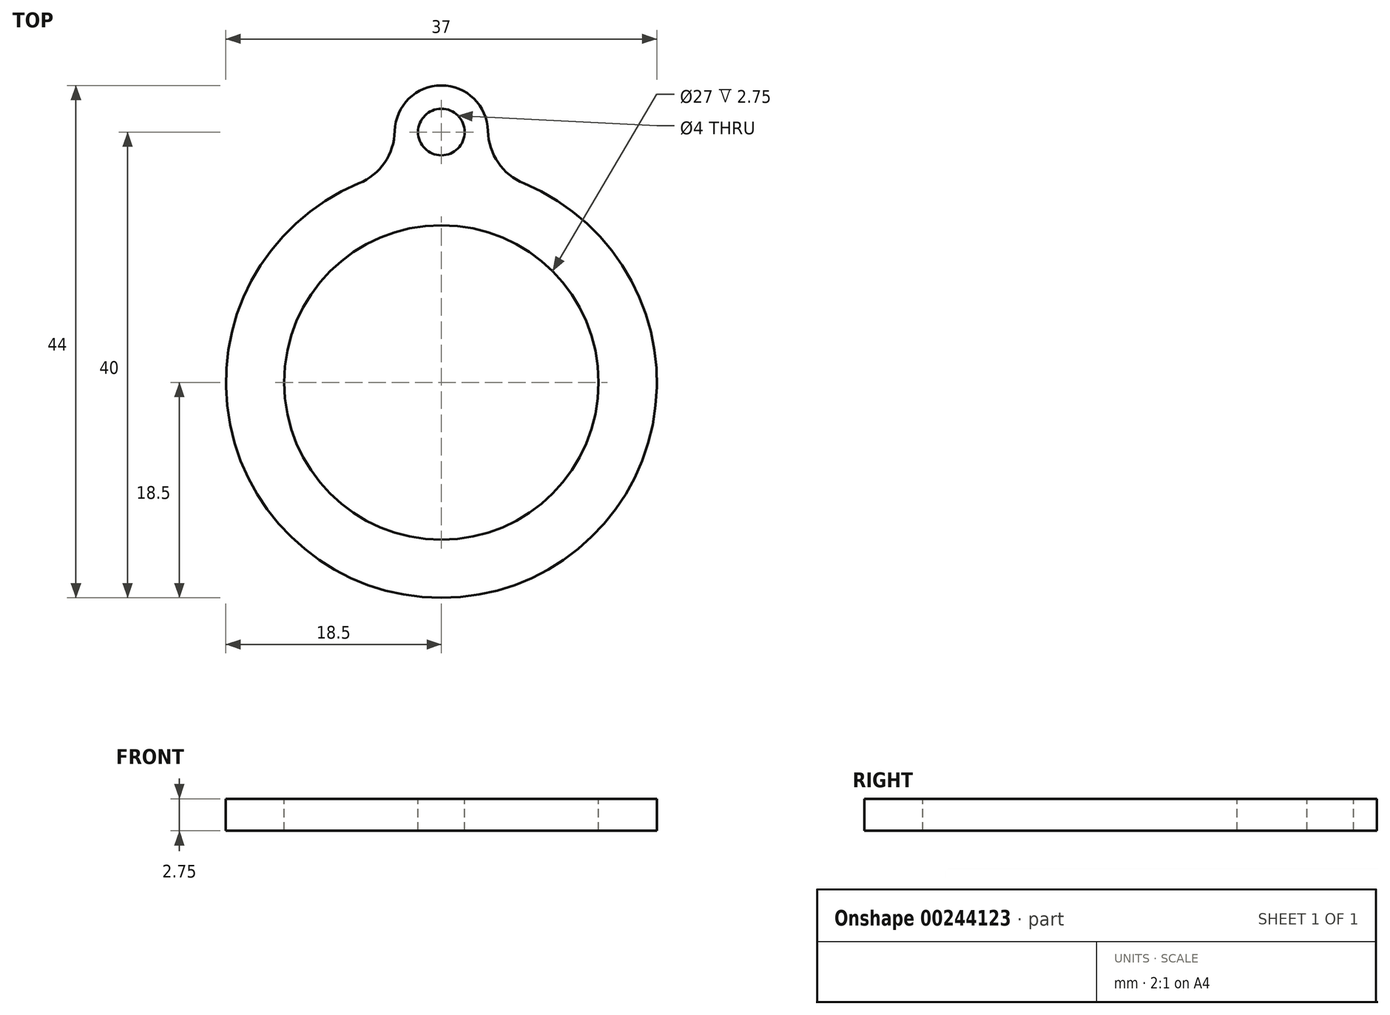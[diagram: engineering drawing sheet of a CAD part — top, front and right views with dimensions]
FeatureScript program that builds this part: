
annotation { "Feature Type Name" : "Feature", "Feature Type Description" : "" }
export const myFeature = defineFeature(function(context is Context, id is Id, definition is map)
    precondition{}
    {
        {
            var Q0;
            Q0=qCreatedBy(makeId("Top.planeOp"),FACE);
            var sketch = newSketch(context, id + "F0", { "sketchPlane" : qUnion([Q0])});
            skCircle(sketch, "E0", {"center": v(0, 0) * mm, "radius": 18.5 * mm});
            skCircle(sketch, "E1", {"center": v(0, 0) * mm, "radius": 13.5 * mm});
            skCircle(sketch, "E2", {"center": v(0, 21.5) * mm, "radius": 4 * mm});
            skLineSegment(sketch, "E3", {"start": v(4, 21.5) * mm, "end": v(4, 18.06) * mm});
            skLineSegment(sketch, "E4", {"start": v(-4, 21.5) * mm, "end": v(-4, 18.06) * mm});
            skCircle(sketch, "E5", {"center": v(0, 21.5) * mm, "radius": 2 * mm});
            skSolve(sketch);
        }
        {
            var Q0;
            Q0=makeQuery(id+"F0.imprint","IMPRINT",FACE,{"disambiguationData":[TD([[makeQuery(id+"F0.imprint","IMPRINT",EDGE,{"derivedFrom":sQuery(id+"F0.wireOp",EDGE,"E1")}),-1.0]])]});
            var Q1;
            {var subQ0=sQuery(id+"F0.wireOp",EDGE,"E2");var subQ1=sQuery(id+"F0.wireOp",EDGE,"E0");var subQ2=makeQuery(id+"F0.imprint","INTERSECT",VERTEX,{"disambiguationData":[OD(0.0)],"derivedFrom":[subQ1,subQ0]});Q1=makeQuery(id+"F0.imprint","IMPRINT",FACE,{"disambiguationData":[TD([[makeQuery(id+"F0.imprint","IMPRINT",EDGE,{"disambiguationData":[TD([[subQ2,-1.0]])],"derivedFrom":subQ1}),1.0]])]});}
            var Q2;
            Q2=makeQuery(id+"F0.imprint","IMPRINT",FACE,{"disambiguationData":[TD([[makeQuery(id+"F0.imprint","IMPRINT",EDGE,{"derivedFrom":sQuery(id+"F0.wireOp",EDGE,"E5")}),-1.0]])]});
            var Q3;
            {var subQ0=sQuery(id+"F0.wireOp",EDGE,"E3");Q3=makeQuery(id+"F0.imprint","IMPRINT",FACE,{"disambiguationData":[TD([[makeQuery(id+"F0.imprint","IMPRINT",EDGE,{"derivedFrom":subQ0}),-1.0]])]});}
            var Q4;
            {var subQ0=sQuery(id+"F0.wireOp",EDGE,"E4");Q4=makeQuery(id+"F0.imprint","IMPRINT",FACE,{"disambiguationData":[TD([[makeQuery(id+"F0.imprint","IMPRINT",EDGE,{"derivedFrom":subQ0}),1.0]])]});}
            extrude(context, id + "F1", {"entities" : qUnion([Q0, Q1, Q2, Q3, Q4]), "oppositeDirection" : true, "depth" : 2.75 * mm});
        }
        {
            var Q0;
            Q0=makeQuery(id+"F1.opExtrude","SWEPT_EDGE",EDGE,{"disambiguationData":[OSD([sQuery(id+"F0.wireOp",EDGE,"E0"),sQuery(id+"F0.wireOp",EDGE,"E3")])]});
            var Q1;
            Q1=makeQuery(id+"F1.opExtrude","SWEPT_EDGE",EDGE,{"disambiguationData":[OSD([sQuery(id+"F0.wireOp",EDGE,"E0"),sQuery(id+"F0.wireOp",EDGE,"E4")])]});
            fillet(context, id + "F2", {"entities" : qUnion([Q0, Q1]), "radius" : 5 * mm, "tangentPropagation" : true, "allowEdgeOverflow" : false});
        }
    });
